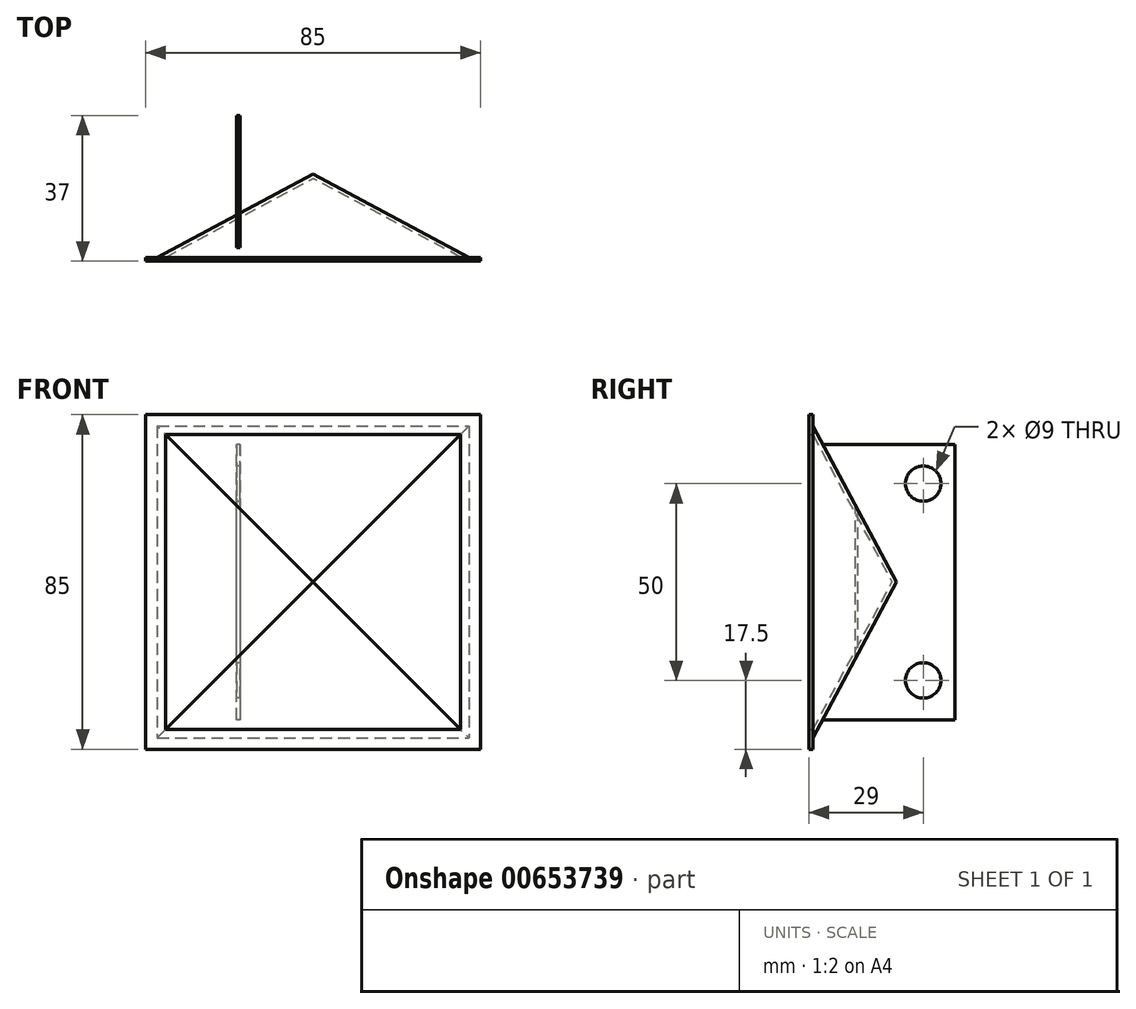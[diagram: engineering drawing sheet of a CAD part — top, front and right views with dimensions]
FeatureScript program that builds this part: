
annotation { "Feature Type Name" : "Feature", "Feature Type Description" : "" }
export const myFeature = defineFeature(function(context is Context, id is Id, definition is map)
    precondition{}
    {
        {
            var Q0;
            Q0=qCreatedBy(makeId("Front.planeOp"),FACE);
            var sketch = newSketch(context, id + "F0", { "sketchPlane" : qUnion([Q0])});
            skLineSegment(sketch, "E0.bottom", {"start": v(42.5, 42.5) * mm, "end": v(-42.5, 42.5) * mm});
            skLineSegment(sketch, "E0.top", {"start": v(42.5, -42.5) * mm, "end": v(-42.5, -42.5) * mm});
            skLineSegment(sketch, "E0.left", {"start": v(42.5, 42.5) * mm, "end": v(42.5, -42.5) * mm});
            skLineSegment(sketch, "E0.right", {"start": v(-42.5, 42.5) * mm, "end": v(-42.5, -42.5) * mm});
            skPoint(sketch, "E0.middle", {"position": v(0, 0) * mm});
            skLineSegment(sketch, "E1.bottom", {"start": v(-37.5, 37.5) * mm, "end": v(37.5, 37.5) * mm});
            skLineSegment(sketch, "E1.top", {"start": v(-37.5, -37.5) * mm, "end": v(37.5, -37.5) * mm});
            skLineSegment(sketch, "E1.left", {"start": v(-37.5, 37.5) * mm, "end": v(-37.5, -37.5) * mm});
            skLineSegment(sketch, "E1.right", {"start": v(37.5, 37.5) * mm, "end": v(37.5, -37.5) * mm});
            skSolve(sketch);
        }
        {
            var Q0;
            Q0=qCreatedBy(makeId("Front.planeOp"),FACE);
            cPlane(context, id + "F1", {"entities" : qUnion([Q0]), "cplaneType" : CPlaneType.OFFSET, "offset" : 20 * mm, "oppositeDirection" : true, "width" : 150 * mm, "height" : 150 * mm});
        }
        {
            var Q0;
            Q0=qCreatedBy(id+"F1.planeOp",FACE);
            var sketch = newSketch(context, id + "F2", { "sketchPlane" : qUnion([Q0])});
            skPoint(sketch, "E2", {"position": v(0, 0) * mm});
            skSolve(sketch);
        }
        {
            var Q0;
            Q0=makeQuery(id+"F0.imprint","IMPRINT",FACE,{"disambiguationData":[TD([[makeQuery(id+"F0.imprint","IMPRINT",EDGE,{"derivedFrom":sQuery(id+"F0.wireOp",EDGE,"E1.bottom")}),-1.0]])]});
            var Q1;
            Q1=sQuery(id+"F2.wireOp",VERTEX,"E2");
            loft(context, id + "F3", {"sheetProfilesArray" : [{ "sheetProfileEntities" : qUnion([Q0]) }, { "sheetProfileEntities" : qUnion([Q1]) }]});
        }
        {
            var Q0;
            Q0=makeQuery(id+"F3.opLoft","CAP_FACE",FACE,{"disambiguationData":[OSD([makeQuery(id+"F0.imprint","IMPRINT",FACE,{"disambiguationData":[TD([[makeQuery(id+"F0.imprint","IMPRINT",EDGE,{"derivedFrom":sQuery(id+"F0.wireOp",EDGE,"E1.bottom")}),-1.0]])]})])],"isStart":true});
            shell(context, id + "F4", {"entities" : qUnion([Q0]), "thickness" : 1 * mm, "oppositeDirection" : true});
        }
        {
            var Q0;
            Q0=makeQuery(id+"F0.imprint","IMPRINT",FACE,{"disambiguationData":[TD([[makeQuery(id+"F0.imprint","IMPRINT",EDGE,{"derivedFrom":sQuery(id+"F0.wireOp",EDGE,"E0.bottom")}),1.0]])]});
            extrude(context, id + "F5", {"entities" : qUnion([Q0]), "operationType" : NewBodyOperationType.ADD, "depth" : 1 * mm});
        }
        {
            var Q0;
            Q0=qCreatedBy(makeId("Front.planeOp"),FACE);
            cPlane(context, id + "F6", {"entities" : qUnion([Q0]), "cplaneType" : CPlaneType.OFFSET, "offset" : 36 * mm, "oppositeDirection" : true, "width" : 150 * mm, "height" : 150 * mm});
        }
        {
            var Q0;
            Q0=qCreatedBy(id+"F6.planeOp",FACE);
            var sketch = newSketch(context, id + "F7", { "sketchPlane" : qUnion([Q0])});
            skLineSegment(sketch, "E3", {"start": v(-19.5, -35) * mm, "end": v(-19.5, 35) * mm});
            skLineSegment(sketch, "E4", {"start": v(-19.5, 35) * mm, "end": v(-18.5, 35) * mm});
            skLineSegment(sketch, "E5", {"start": v(-18.5, 35) * mm, "end": v(-18.5, -35) * mm});
            skLineSegment(sketch, "E6", {"start": v(-18.5, -35) * mm, "end": v(-19.5, -35) * mm});
            skSolve(sketch);
        }
        {
            var Q0;
            Q0=qSketchRegion(id+"F7",true);
            extrude(context, id + "F8", {"entities" : qUnion([Q0]), "operationType" : NewBodyOperationType.ADD, "endBound" : BoundingType.UP_TO_NEXT, "depth" : 25 * mm});
        }
        {
            var Q0;
            Q0=makeQuery(id+"F8.opExtrude","SWEPT_FACE",FACE,{"disambiguationData":[OSD([sQuery(id+"F7.wireOp",EDGE,"E3")])]});
            var sketch = newSketch(context, id + "F9", { "sketchPlane" : qUnion([Q0])});
            skCircle(sketch, "E7", {"center": v(-28, -25) * mm, "radius": 4.5 * mm});
            skCircle(sketch, "E8", {"center": v(-28, 25) * mm, "radius": 4.5 * mm});
            skSolve(sketch);
        }
        {
            var Q0;
            Q0=qSketchRegion(id+"F9",true);
            extrude(context, id + "F10", {"entities" : qUnion([Q0]), "operationType" : NewBodyOperationType.REMOVE, "endBound" : BoundingType.THROUGH_ALL, "oppositeDirection" : true, "depth" : 25 * mm});
        }
    });
